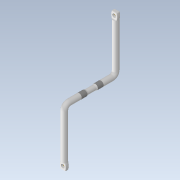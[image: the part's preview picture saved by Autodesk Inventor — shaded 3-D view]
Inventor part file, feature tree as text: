
AUTODESK INVENTOR PART (.ipt)
format: ipt  version: 2021 (Build 250183000, 183)  size: 1,539,584 bytes
history: native  units: mm
features: sketch x14, other x5, plane x4, fillet x3, thread x2, sweep x2, loft x2, hole x2, revolve x1
ambient origin geometry x8: Origin, YZ Plane, XZ Plane, XY Plane, X Axis, Y Axis, Z Axis, Center Point
bodies: Body1 (feature_tree)
feature tree (35):
  other  "Sólido1"
  revolve  "Revolución1"  [1 undecoded]
  thread  "Rosca1"  [1 undecoded]
  thread  "Rosca2"  [1 undecoded]
  sketch  "Boceto2"  dims[d9=25.0mm d10=0.0mm d14=2100.0mm]
  sketch  "Boceto4"  dims[d24=190.678642mm d25=190.678642mm]
  other  "Punto de trabajo1"
  sketch  "Boceto5"  dims[d32=20.0mm d33=15.0mm d34=230.0mm]
  sweep  "Barrido1"
  sketch  "Boceto8"  dims[d39=0.0mm d40=0.0mm d42=40.0mm]
  sweep  "Barrido2"
  plane  "Plano de trabajo2"
  sketch  "Boceto10"  dims[d43=20.0mm d45=27.0mm d46=14.0mm]
  plane  "Plano de trabajo3"
  loft  "Solevación3"
  fillet  "Empalme1"  Radius=230.0mm
  other  "Punto de trabajo2"
  hole  "Agujero1"  [1 undecoded]
  fillet  "Empalme2"  Radius=15.0mm
  plane  "Plano de trabajo5"
  loft  "Solevación4"
  other  "Punto de trabajo3"
  hole  "Agujero2"  [1 undecoded]
  fillet  "Empalme3"  Radius=14.0mm
  sketch  "Boceto1"  dims[d4=90.0deg d5=24.0mm d6=20.0mm d7=25.0mm d8=0.0mm]
  other  "Imagen1"
  sketch  "Boceto6"  dims[d35=0.0mm d36=0.0mm d37=230.0mm d38=15.0mm]
  sketch  "Boceto11"  dims[d47=15.0mm]
  sketch  "Boceto12"  dims[d59=14.0mm]
  sketch  "Boceto13"  dims[d67=14.0mm]
  plane  "Plano de trabajo4"
  sketch  "Boceto14"  dims[d68=0.0mm d69=90.0deg]
  sketch  "Boceto15"  dims[d70=0.0mm d71=90.0deg]
  sketch  "Boceto16"  dims[d72=0.0mm d73=90.0deg]
  sketch  "Boceto17"  dims[d74=2.0mm d75=16.0mm d76=32.0mm d77=4.0mm d78=2.0mm d79=90.0deg d80=8.0mm d81=20.594885mm d82=2.0mm d83=15.0mm d84=27.0mm d85=14.0mm d86=14.0mm d87=14.0mm d88=0.0mm d89=90.0deg d90=0.0mm d91=90.0deg d92=0.0mm d93=90.0deg d94=16.0mm d95=32.0mm d96=27.25mm d97=9.25mm d98=90.0deg d99=8.0mm d100=20.594885mm d101=2.0mm]
note: 5 required parameter values undecoded (feature->parameter linkage not recoverable at this tier; creation-order binding heuristic only, values carry confidence <= 0.55)